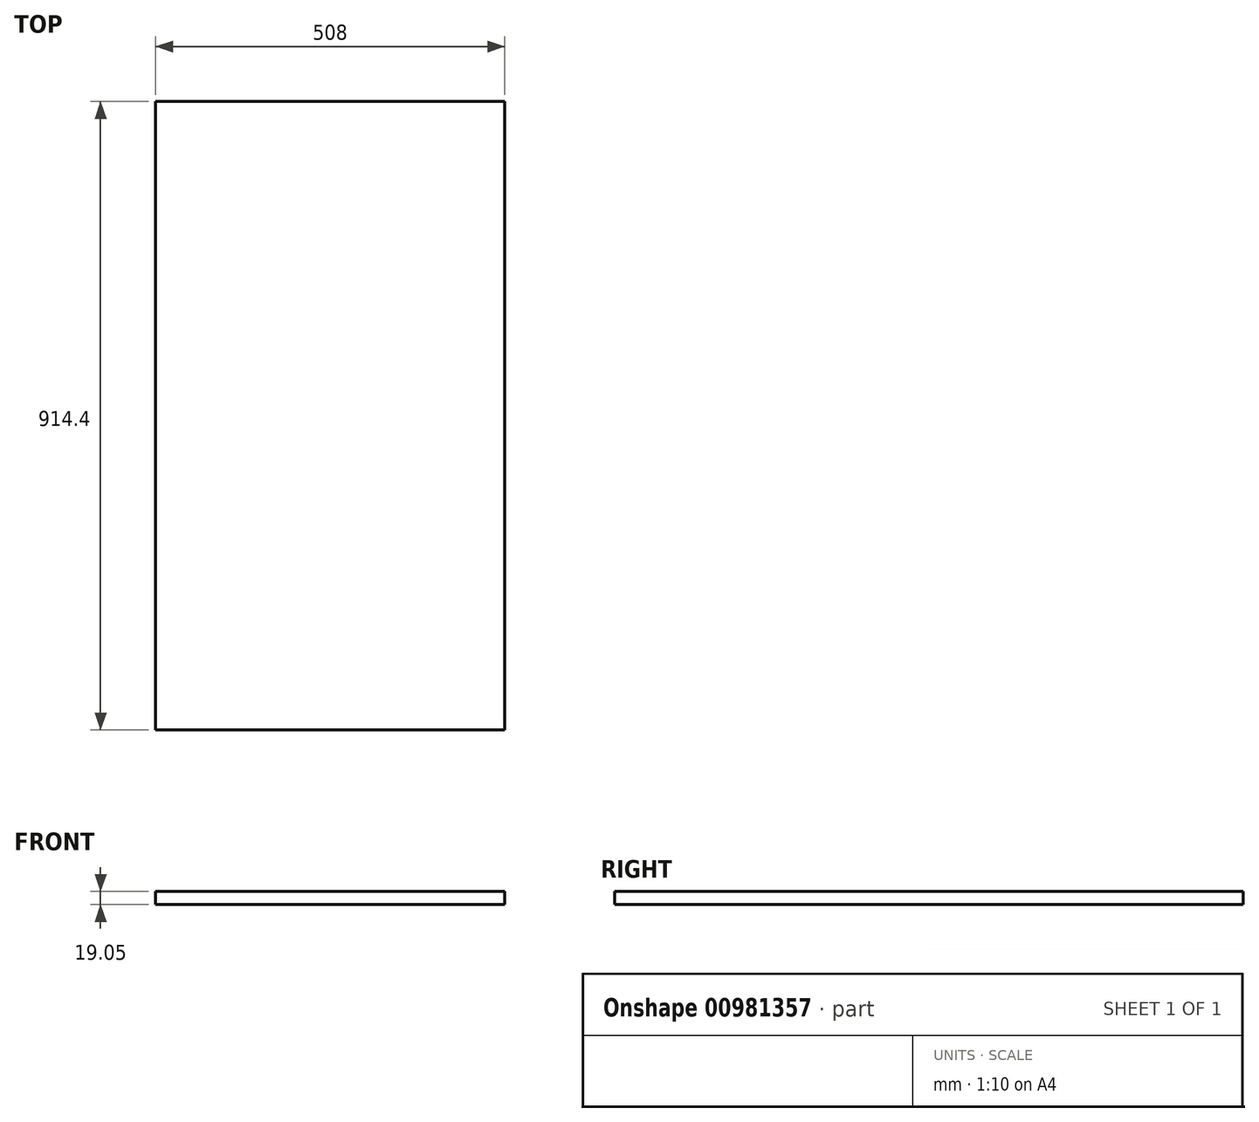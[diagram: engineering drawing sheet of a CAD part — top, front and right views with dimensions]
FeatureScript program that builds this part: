
annotation { "Feature Type Name" : "Feature", "Feature Type Description" : "" }
export const myFeature = defineFeature(function(context is Context, id is Id, definition is map)
    precondition{}
    {
        {
            var Q0;
            Q0=qCreatedBy(makeId("Top.planeOp"),FACE);
            var sketch = newSketch(context, id + "F0", { "sketchPlane" : qUnion([Q0])});
            skLineSegment(sketch, "E0.bottom", {"start": v(254, 457.2) * mm, "end": v(-254, 457.2) * mm});
            skLineSegment(sketch, "E0.top", {"start": v(254, -457.2) * mm, "end": v(-254, -457.2) * mm});
            skLineSegment(sketch, "E0.left", {"start": v(254, 457.2) * mm, "end": v(254, -457.2) * mm});
            skLineSegment(sketch, "E0.right", {"start": v(-254, 457.2) * mm, "end": v(-254, -457.2) * mm});
            skPoint(sketch, "E0.middle", {"position": v(0, 0) * mm});
            skSolve(sketch);
        }
        {
            var Q0;
            Q0=makeQuery(id+"F0.imprint","IMPRINT",FACE,{"disambiguationData":[TD([[makeQuery(id+"F0.imprint","IMPRINT",EDGE,{"derivedFrom":sQuery(id+"F0.wireOp",EDGE,"E0.bottom")}),1.0]])]});
            extrude(context, id + "F1", {"entities" : qUnion([Q0]), "depth" : 19.05 * mm, "offsetDistance" : 25.4 * mm});
        }
    });
